# Revit family: Комби-клапан – регулятор расхода 4206_R_SMART_LF_MF
name_source: partatom
category: Rohrzubehör
revit_build: Autodesk Revit 2018 (Build: 20190510_1515(x64)
units: mm (PartAtom-declared; Revit-internal decimal feet)

## family parameters
Arbeitsebenenbasiert = Nein
Beim Laden mit Abzugskörper schneiden = Nein
Bemaßung runder Anschluss = Durchmesser verwenden
Gemeinsam genutzt = Nein
Immer vertikal = Ja
OmniClass-Nummer = 23.65.55.14
OmniClass-Titel = Valves for Liquid Services
Teiletyp = Unterbricht

## types (2) — shared parameters
B01 = 41.62 mm  [stored 0.136549 ft]
B03 = 7.93 mm  [stored 0.0260171 ft]
B04 = 6.75 mm  [stored 0.0221457 ft]
B05 = 3.7 mm  [stored 0.0121391 ft]
B06 = 5.86 mm  [stored 0.0192257 ft]
B08 = 23.05 mm  [stored 0.0756234 ft]
B10 = 31.75 mm
B11 = 34.69 mm
B12 = 36.73 mm
B13 = 40.79 mm  [stored 0.133825 ft]
B14 = 8.73 mm  [stored 0.0286417 ft]
B15 = 23 mm  [stored 0.0754593 ft]
B16 = 26 mm
H01 = 35 mm  [stored 0.114829 ft]
H03 = 3.46 mm  [stored 0.0113517 ft]
H04 = 6.74 mm  [stored 0.0221129 ft]
H05 = 10.06 mm  [stored 0.0330052 ft]
H06 = 24.02 mm  [stored 0.0788058 ft]
H07 = 28.19 mm  [stored 0.0924869 ft]
H08 = 4.24 mm  [stored 0.0139108 ft]
H09 = 1.08 mm
H10 = 22.33 mm  [stored 0.0732612 ft]
Hersteller = Herz-Armaturen GmbH
L01 = 41 mm  [stored 0.134514 ft]
L02 = 34 mm
L05 = 3.44 mm  [stored 0.0112861 ft]
L06 = 3.44 mm  [stored 0.0112861 ft]
L13 = 32 mm  [stored 0.104987 ft]
L14 = 44 mm  [stored 0.144357 ft]
PN = 25
SCRNCODE = 05;04;02
SCRNSEQ = ARM;ARM_TYP="DURR";2
URL = www.herz-armaturen.ru
Защитный колпачок = Пластик
Импульсная трубка = Медь Cu-DHP (CW024A)
Кольцевое уплотнение O-Ring = EPDM
Корпус = Латунь, устойчивая к селективной цинковой коррозии
Корпус мембраны = Латунь CW602N
Макс. перепад давления = 400000.0 Pa
Макс. рабочая температура до DN32 = 130 °C
Макс. рабочая температура от DN40 = 110 °C
Макс. рабочее давление = 1600000.0 Pa
Мембрана = EPDM
Мин. рабочая температура (антифриз) = -20 °C
Мин. рабочая температура (чистая вода) = 2 °C
Область применения = Комби-клапан применяется в системах отопления и охлаждения с насосами. Комби-клапан автоматически ограничивает расход на выбранном участке системы до заданного значения, компенсируя все колебания давления. При этом нет необходимости в измерениях, а регулирование эффективно при любых условиях эксплуатации. Комби-клапан регулирует расход в соответствии с настройкой до заданного значения; на мембрану воздействует давление непосредственно до и после регулирующей части.
Пружина = Пружинная нержавеющая сталь
Среда = Качество теплоносителя в соответствии с ÖNORM H5195 и/или предписаниями VDI-Standard 2035.
Разрешается использование смеси этилен- или пропиленгликоля в соотношении 25-50% с водой.
Ход = 4 mm  [stored 0.0131234 ft]
Шпиндель = Нержавеющая сталь 14301

## type names (no varying parameters)
- LF
- MF

note: [stored X ft] marks values corroborated as IEEE doubles in the binary element streams (Revit-internal decimal feet)
